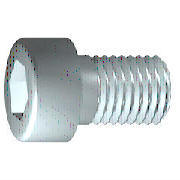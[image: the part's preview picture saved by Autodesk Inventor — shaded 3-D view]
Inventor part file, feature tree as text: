
AUTODESK INVENTOR PART (.ipt)
format: ipt  version: 2016 SP1 (Build 200210100, 210)  size: 198,144 bytes
history: native  units: mm (DEFAULTED — no unit token found)
features: sketch x2, extrude x1, plane x1, fillet x1
ambient origin geometry x7: Origin, YZ Plane, XY Plane, X Axis, Y Axis, Z Axis, Center Point
bodies: Solid1 (feature_tree), Body (feature_tree)
feature tree (5):
  extrude  "Slot"  Depth=2.8448mm
  plane  "Work Plane1"
  fillet  "Fillet2"  Radius=2.8448mm
  sketch  "Sketch1"  dims[d1=5.49275mm d2=1.5876mm d3=2.8448mm]
  sketch  "Sketch2"  dims[d4=1.2954mm d5=60.0deg d6=2.8448mm d7=2.8448mm d8=2.756963mm d9=4.6482mm d10=90.0deg d11=10.0mm d12=0.0mm d13=5.49275mm d14=0.0mm d15=0.37846mm d16=0.37846mm d17=0.2286mm d19=0.0mm d26=7.9375mm d27=45.0deg d28=0.0mm d29=0.0mm d30=0.1016mm]
